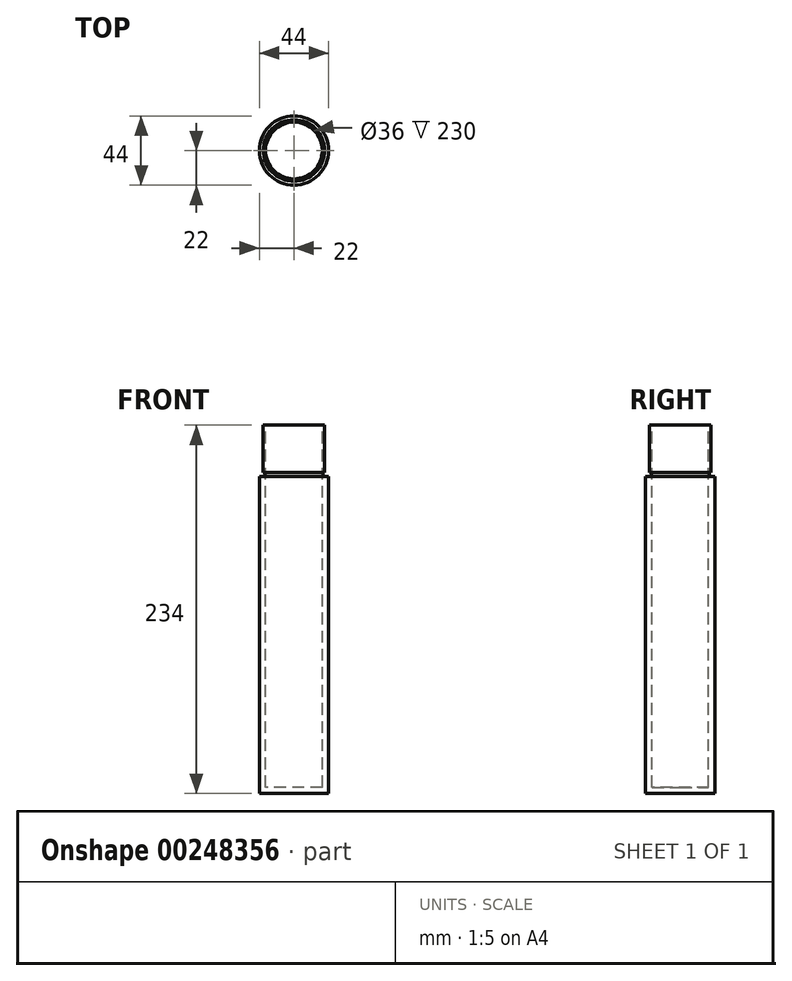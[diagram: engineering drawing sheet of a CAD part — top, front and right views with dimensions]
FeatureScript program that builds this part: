
annotation { "Feature Type Name" : "Feature", "Feature Type Description" : "" }
export const myFeature = defineFeature(function(context is Context, id is Id, definition is map)
    precondition{}
    {
        {
            var Q0;
            Q0=qCreatedBy(makeId("Front.planeOp"),FACE);
            var sketch = newSketch(context, id + "F0", { "sketchPlane" : qUnion([Q0])});
            skLineSegment(sketch, "E0", {"start": v(0, 0) * mm, "end": v(22, 0) * mm});
            skLineSegment(sketch, "E1", {"start": v(22, 0) * mm, "end": v(22, 201.5) * mm});
            skLineSegment(sketch, "E2", {"start": v(22, 201.5) * mm, "end": v(18.4, 201.5) * mm});
            skLineSegment(sketch, "E3", {"start": v(18.4, 201.5) * mm, "end": v(18.4, 204) * mm});
            skLineSegment(sketch, "E4", {"start": v(18.4, 204) * mm, "end": v(19.5, 204) * mm});
            skLineSegment(sketch, "E5", {"start": v(19.5, 204) * mm, "end": v(19.5, 234) * mm});
            skLineSegment(sketch, "E6", {"start": v(19.5, 234) * mm, "end": v(0, 234) * mm});
            skLineSegment(sketch, "E7", {"start": v(0, 234) * mm, "end": v(0, 0) * mm});
            skSolve(sketch);
        }
        {
            var Q0;
            Q0=makeQuery(id+"F0.imprint","IMPRINT",FACE,{"disambiguationData":[TD([[makeQuery(id+"F0.imprint","IMPRINT",EDGE,{"derivedFrom":sQuery(id+"F0.wireOp",EDGE,"E0")}),1.0]])]});
            var Q1;
            Q1=sQuery(id+"F0.wireOp",EDGE,"E7");
            revolve(context, id + "F1", {"entities" : qUnion([Q0]), "axis" : qUnion([Q1]), "revolveType" : RevolveType.FULL});
        }
        {
            var Q0;
            Q0=makeQuery(id+"F1.opRevolve","SWEPT_FACE",FACE,{"disambiguationData":[OSD([sQuery(id+"F0.wireOp",EDGE,"E6")])]});
            var sketch = newSketch(context, id + "F2", { "sketchPlane" : qUnion([Q0])});
            skCircle(sketch, "E8", {"center": v(0, 0) * mm, "radius": 20 * mm});
            skSolve(sketch);
        }
        {
            var Q0;
            Q0=makeQuery(id+"F2.imprint","IMPRINT",FACE,{"disambiguationData":[TD([[makeQuery(id+"F2.imprint","IMPRINT",EDGE,{"derivedFrom":makeQuery(id+"F1.opRevolve","SWEPT_EDGE",EDGE,{"disambiguationData":[OSD([sQuery(id+"F0.wireOp",EDGE,"E5"),sQuery(id+"F0.wireOp",EDGE,"E6")])]})}),1.0]])]});
            var sketch = newSketch(context, id + "F3", { "sketchPlane" : qUnion([Q0])});
            skCircle(sketch, "E9", {"center": v(0, 0) * mm, "radius": 18 * mm});
            skSolve(sketch);
        }
        {
            var Q0;
            Q0 = qSketchRegion(id + "F3", true);
            extrude(context, id + "F4", {"entities" : qUnion([Q0]), "operationType" : NewBodyOperationType.REMOVE, "oppositeDirection" : true, "depth" : 230 * mm});
        }
    });
